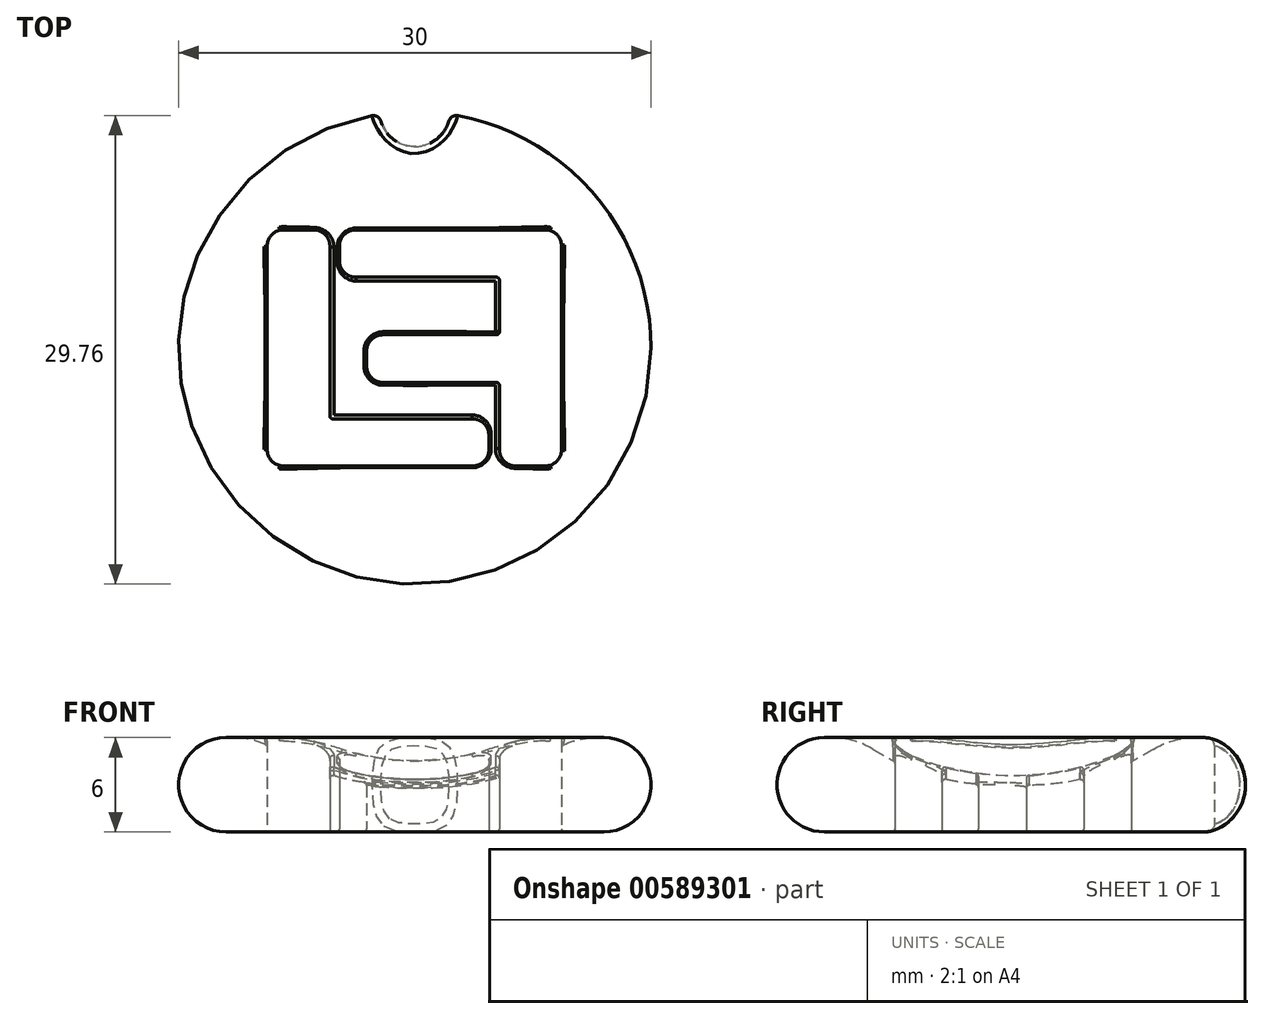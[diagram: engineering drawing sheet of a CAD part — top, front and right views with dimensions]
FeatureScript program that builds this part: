
annotation { "Feature Type Name" : "Feature", "Feature Type Description" : "" }
export const myFeature = defineFeature(function(context is Context, id is Id, definition is map)
    precondition{}
    {
        {
            var Q0;
            Q0=qCreatedBy(makeId("Front.planeOp"),FACE);
            var sketch = newSketch(context, id + "F0", { "sketchPlane" : qUnion([Q0])});
            skLineSegment(sketch, "E0", {"start": v(0, 0) * mm, "end": v(-12, 0) * mm});
            skLineSegment(sketch, "E1", {"start": v(-12, 12.25) * mm, "end": v(-12, -7.94) * mm, "construction": true});
            skPoint(sketch, "E2", {"position": v(-12, 3) * mm});
            skArc(sketch, "E3", {"start": v(-12, 6) * mm, "mid": v(-15, 3) * mm, "end": v(-12, 0) * mm});
            skLineSegment(sketch, "E4", {"start": v(-12, 6) * mm, "end": v(-10, 6) * mm});
            skPoint(sketch, "E5", {"position": v(0, 3) * mm});
            skArc(sketch, "E6", {"start": v(-10, 6) * mm, "mid": v(-5.27, 3.6) * mm, "end": v(0, 3) * mm});
            skLineSegment(sketch, "E7", {"start": v(0, 3) * mm, "end": v(0, 0) * mm});
            skSolve(sketch);
        }
        {
            var Q0;
            Q0=makeQuery(id+"F0.imprint","IMPRINT",FACE,{"disambiguationData":[TD([[makeQuery(id+"F0.imprint","IMPRINT",EDGE,{"derivedFrom":sQuery(id+"F0.wireOp",EDGE,"E0")}),-1.0]])]});
            var Q1;
            Q1=sQuery(id+"F0.wireOp",EDGE,"E7");
            revolve(context, id + "F1", {"entities" : qUnion([Q0]), "axis" : qUnion([Q1]), "revolveType" : RevolveType.FULL});
        }
        {
            var Q0;
            Q0=makeQuery(id+"F1.opRevolve","SWEPT_EDGE",EDGE,{"disambiguationData":[OSD([sQuery(id+"F0.wireOp",EDGE,"E4"),sQuery(id+"F0.wireOp",EDGE,"E6")])]});
            fillet(context, id + "F2", {"entities" : qUnion([Q0]), "radius" : 5 * mm, "tangentPropagation" : true, "allowEdgeOverflow" : false});
        }
        {
            var Q0;
            Q0=qCreatedBy(makeId("Top.planeOp"),FACE);
            var sketch = newSketch(context, id + "F3", { "sketchPlane" : qUnion([Q0])});
            skLineSegment(sketch, "E8", {"start": v(3.67, -4.51) * mm, "end": v(-5.4, -4.51) * mm});
            skArc(sketch, "E9", {"start": v(4.7, -5.54) * mm, "mid": v(4.4, -4.81) * mm, "end": v(3.67, -4.51) * mm});
            skLineSegment(sketch, "E10", {"start": v(4.7, -6.47) * mm, "end": v(4.7, -5.54) * mm});
            skArc(sketch, "E11", {"start": v(3.67, -7.5) * mm, "mid": v(4.4, -7.2) * mm, "end": v(4.7, -6.47) * mm});
            skLineSegment(sketch, "E12", {"start": v(-8.35, -7.5) * mm, "end": v(3.67, -7.5) * mm});
            skArc(sketch, "E13", {"start": v(-9.38, -6.47) * mm, "mid": v(-9.08, -7.2) * mm, "end": v(-8.35, -7.5) * mm});
            skArc(sketch, "E14", {"start": v(-8.35, 7.5) * mm, "mid": v(-9.08, 7.2) * mm, "end": v(-9.38, 6.47) * mm});
            skLineSegment(sketch, "E15", {"start": v(-6.43, 7.5) * mm, "end": v(-8.35, 7.5) * mm});
            skLineSegment(sketch, "E16", {"start": v(-5.4, -4.51) * mm, "end": v(-5.4, 6.47) * mm});
            skArc(sketch, "E17", {"start": v(-5.4, 6.47) * mm, "mid": v(-5.7, 7.2) * mm, "end": v(-6.43, 7.5) * mm});
            skLineSegment(sketch, "E18", {"start": v(-9.38, 6.47) * mm, "end": v(-9.38, -6.47) * mm});
            skArc(sketch, "E19", {"start": v(8.29, -7.5) * mm, "mid": v(9.02, -7.2) * mm, "end": v(9.32, -6.47) * mm});
            skLineSegment(sketch, "E20", {"start": v(6.4, -7.5) * mm, "end": v(8.29, -7.5) * mm});
            skArc(sketch, "E21", {"start": v(5.37, -6.47) * mm, "mid": v(5.68, -7.2) * mm, "end": v(6.4, -7.5) * mm});
            skLineSegment(sketch, "E22", {"start": v(5.37, -2.2) * mm, "end": v(5.37, -6.47) * mm});
            skLineSegment(sketch, "E23", {"start": v(-2.03, -2.2) * mm, "end": v(5.37, -2.2) * mm});
            skArc(sketch, "E24", {"start": v(-3.06, -1.16) * mm, "mid": v(-2.76, -1.9) * mm, "end": v(-2.03, -2.2) * mm});
            skLineSegment(sketch, "E25", {"start": v(-3.06, -0.2) * mm, "end": v(-3.06, -1.16) * mm});
            skArc(sketch, "E26", {"start": v(-2.03, 0.83) * mm, "mid": v(-2.76, 0.53) * mm, "end": v(-3.06, -0.2) * mm});
            skLineSegment(sketch, "E27", {"start": v(5.37, 0.83) * mm, "end": v(-2.03, 0.83) * mm});
            skArc(sketch, "E28", {"start": v(-3.76, 7.5) * mm, "mid": v(-4.49, 7.2) * mm, "end": v(-4.79, 6.47) * mm});
            skArc(sketch, "E29", {"start": v(9.32, 6.47) * mm, "mid": v(9.02, 7.2) * mm, "end": v(8.29, 7.5) * mm});
            skArc(sketch, "E30", {"start": v(-4.79, 5.52) * mm, "mid": v(-4.49, 4.8) * mm, "end": v(-3.76, 4.5) * mm});
            skLineSegment(sketch, "E31", {"start": v(5.37, 4.5) * mm, "end": v(5.37, 0.83) * mm});
            skLineSegment(sketch, "E32", {"start": v(-3.76, 4.5) * mm, "end": v(5.37, 4.5) * mm});
            skLineSegment(sketch, "E33", {"start": v(-4.79, 6.47) * mm, "end": v(-4.79, 5.52) * mm});
            skLineSegment(sketch, "E34", {"start": v(8.29, 7.5) * mm, "end": v(-3.76, 7.5) * mm});
            skLineSegment(sketch, "E35", {"start": v(9.32, -6.47) * mm, "end": v(9.32, 6.47) * mm});
            skSolve(sketch);
        }
        {
            var Q0;
            Q0 = qSketchRegion(id + "F3", true);
            extrude(context, id + "F4", {"entities" : qUnion([Q0]), "operationType" : NewBodyOperationType.REMOVE, "depth" : 25 * mm, "offsetDistance" : 25 * mm});
        }
        {
            var Q0;
            Q0=makeQuery(id+"F4.boolean.opBoolean","INTERSECT",EDGE,{"derivedFrom":[makeQuery(id+"F2.opFillet","BLEND_FACE",FACE,{"disambiguationData":[OSD([sQuery(id+"F0.wireOp",EDGE,"E4"),sQuery(id+"F0.wireOp",EDGE,"E6")])]}),makeQuery(id+"F4.opExtrude","SWEPT_FACE",FACE,{"disambiguationData":[OSD([sQuery(id+"F3.wireOp",EDGE,"E18")])]})]});
            var Q1;
            Q1=makeQuery(id+"F4.boolean.opBoolean","COPY",FACE,{"derivedFrom":makeQuery(id+"F4.opExtrude","SWEPT_FACE",FACE,{"disambiguationData":[OSD([sQuery(id+"F3.wireOp",EDGE,"E27")])]})});
            var Q2;
            Q2=makeQuery(id+"F4.boolean.opBoolean","COPY",FACE,{"derivedFrom":makeQuery(id+"F4.opExtrude","SWEPT_FACE",FACE,{"disambiguationData":[OSD([sQuery(id+"F3.wireOp",EDGE,"E34")])]})});
            var Q3;
            Q3=makeQuery(id+"F4.boolean.opBoolean","COPY",FACE,{"derivedFrom":makeQuery(id+"F4.opExtrude","SWEPT_FACE",FACE,{"disambiguationData":[OSD([sQuery(id+"F3.wireOp",EDGE,"E31")])]})});
            var Q4;
            Q4=makeQuery(id+"F4.boolean.opBoolean","COPY",EDGE,{"derivedFrom":makeQuery(id+"F4.opExtrude","CAP_EDGE",EDGE,{"disambiguationData":[OSD([sQuery(id+"F3.wireOp",EDGE,"E18")])],"isStart":true})});
            var Q5;
            Q5=makeQuery(id+"F4.boolean.opBoolean","COPY",EDGE,{"derivedFrom":makeQuery(id+"F4.opExtrude","SWEPT_EDGE",EDGE,{"disambiguationData":[OSD([sQuery(id+"F3.wireOp",EDGE,"E8"),sQuery(id+"F3.wireOp",EDGE,"E16")])]})});
            var Q6;
            Q6=makeQuery(id+"F4.boolean.opBoolean","COPY",EDGE,{"derivedFrom":makeQuery(id+"F4.opExtrude","SWEPT_EDGE",EDGE,{"disambiguationData":[OSD([sQuery(id+"F3.wireOp",EDGE,"E22"),sQuery(id+"F3.wireOp",EDGE,"E23")])]})});
            fillet(context, id + "F5", {"entities" : qUnion([Q0, Q1, Q2, Q3, Q4, Q5, Q6]), "radius" : .2 * mm, "tangentPropagation" : true, "allowEdgeOverflow" : false});
        }
        {
            var Q0;
            Q0=qCreatedBy(makeId("Top.planeOp"),FACE);
            var sketch = newSketch(context, id + "F6", { "sketchPlane" : qUnion([Q0])});
            skCircle(sketch, "E36", {"center": v(0, 15.04) * mm, "radius": 2.25 * mm});
            skSolve(sketch);
        }
        {
            var Q0;
            Q0=makeQuery(id+"F6.imprint","IMPRINT",FACE,{"disambiguationData":[TD([[makeQuery(id+"F6.imprint","IMPRINT",EDGE,{"derivedFrom":sQuery(id+"F6.wireOp",EDGE,"E36")}),1.0]])]});
            extrude(context, id + "F7", {"entities" : qUnion([Q0]), "operationType" : NewBodyOperationType.REMOVE, "depth" : 25 * mm, "offsetDistance" : 25 * mm});
        }
        {
            var Q0;
            Q0=makeQuery(id+"F7.boolean.opBoolean","INTERSECT",EDGE,{"derivedFrom":[makeQuery(id+"F1.opRevolve","SWEPT_FACE",FACE,{"disambiguationData":[OSD([sQuery(id+"F0.wireOp",EDGE,"E3")])]}),makeQuery(id+"F7.opExtrude","SWEPT_FACE",FACE,{"disambiguationData":[OSD([sQuery(id+"F6.wireOp",EDGE,"E36")])]})]});
            fillet(context, id + "F8", {"entities" : qUnion([Q0]), "radius" : .5 * mm, "tangentPropagation" : true, "allowEdgeOverflow" : false});
        }
    });
